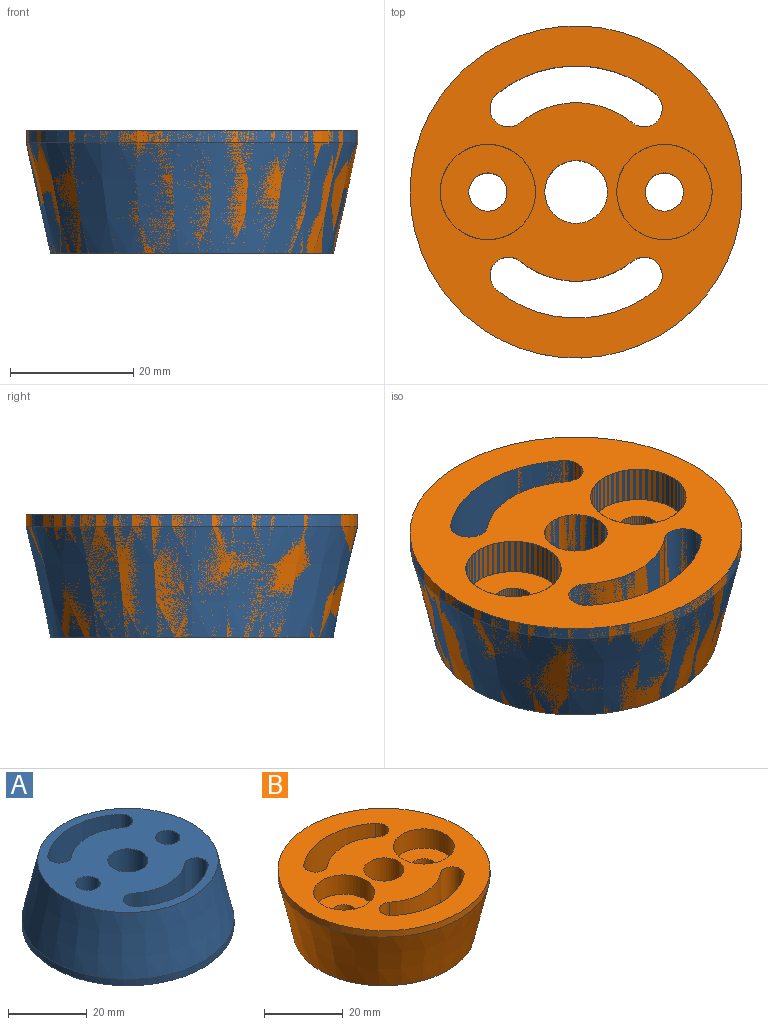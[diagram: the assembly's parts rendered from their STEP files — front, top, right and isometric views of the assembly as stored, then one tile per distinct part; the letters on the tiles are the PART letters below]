
ASSEMBLY  parts=2 mates=1
PART A: 37 faces, bbox 54x54x20 mm
  f0: plane 54x54mm, normal (0,0,-1), area 1488.9mm2, adj f6,f7,f25,f26,f27,f28,f29,f30
  f1: cylinder r=3.1mm len=6.2mm, axis (0,0,1), area 72.1mm2, adj f24,f36
  f2: cylinder r=3.1mm len=6.2mm, axis (0,0,1), area 72.1mm2, adj f10,f33
  f3: cylinder r=3.1mm len=6.2mm, axis (0,0,1), area 97.4mm2, adj f5,f23
  f4: cylinder r=3.1mm len=6.2mm, axis (0,0,1), area 97.4mm2, adj f5,f9
  f5: plane 46x46mm, normal (0,0,1), area 1177.6mm2, adj f3,f4,f6,f8,f25,f26,f27,f28
  f6: cylinder r=5.1mm len=20mm, axis (0,0,-1), area 640.9mm2, adj f0,f5
  f7: cylinder r=27mm len=54mm, axis (0,0,-1), area 339.3mm2, adj f0,f8
  f8: cone r=27mm half-angle=12.5deg, axis (0,0,-1), area 2896.4mm2, adj f5,f7
  f9: plane 11.78x10.2mm, normal (0,0,-1), area 59.9mm2, adj f4,f11,f12,f13,f14,f15,f16
  f10: plane 11.78x10.2mm, normal (0,0,1), area 59.9mm2, adj f2,f11,f12,f13,f14,f15,f16
  f11: plane 5.89x5.3mm, normal (-1,0,0), area 31.2mm2, adj f9,f10,f12,f16
  f12: plane 5.3x5.1mm, normal (-0.5,0.87,0), area 31.2mm2, adj f9,f10,f11,f13
  f13: plane 5.3x5.1mm, normal (0.5,0.87,0), area 31.2mm2, adj f9,f10,f12,f14
  f14: plane 5.89x5.3mm, normal (1,0,0), area 31.2mm2, adj f9,f10,f13,f15
  f15: plane 5.3x5.1mm, normal (0.5,-0.87,0), area 31.2mm2, adj f9,f10,f14,f16
  f16: plane 5.3x5.1mm, normal (-0.5,-0.87,0), area 31.2mm2, adj f9,f10,f11,f15
  f17: plane 5.3x5.1mm, normal (-0.5,-0.87,0), area 31.2mm2, adj f18,f22,f23,f24
  f18: plane 5.89x5.3mm, normal (-1,0,0), area 31.2mm2, adj f17,f19,f23,f24
  f19: plane 5.3x5.1mm, normal (-0.5,0.87,0), area 31.2mm2, adj f18,f20,f23,f24
  f20: plane 5.3x5.1mm, normal (0.5,0.87,0), area 31.2mm2, adj f19,f21,f23,f24
  f21: plane 5.89x5.3mm, normal (1,0,0), area 31.2mm2, adj f20,f22,f23,f24
  f22: plane 5.3x5.1mm, normal (0.5,-0.87,0), area 31.2mm2, adj f17,f21,f23,f24
  f23: plane 11.78x10.2mm, normal (0,0,-1), area 59.9mm2, adj f3,f17,f18,f19,f20,f21,f22
  f24: plane 11.78x10.2mm, normal (0,0,1), area 59.9mm2, adj f1,f17,f18,f19,f20,f21,f22
  f25: cylinder r=14.5mm len=20mm, axis (0,0,-1), area 394.5mm2, adj f0,f5,f26,f28
  f26: cylinder r=3mm len=20mm, axis (0,0,-1), area 188.5mm2, adj f0,f5,f25,f27
  f27: cylinder r=20.5mm len=25.79mm, axis (0,0,-1), area 557.8mm2, adj f0,f5,f26,f28
  f28: cylinder r=3mm len=20mm, axis (0,0,-1), area 188.5mm2, adj f0,f5,f25,f27
  f29: cylinder r=14.5mm len=20mm, axis (0,0,-1), area 394.5mm2, adj f0,f5,f30,f32
  f30: cylinder r=3mm len=20mm, axis (0,0,-1), area 188.5mm2, adj f0,f5,f29,f31
  f31: cylinder r=20.5mm len=25.79mm, axis (0,0,-1), area 557.8mm2, adj f0,f5,f30,f32
  f32: cylinder r=3mm len=20mm, axis (0,0,-1), area 188.5mm2, adj f0,f5,f29,f31
  f33: plane 15.5x15.5mm, normal (0,0,-1), area 158.5mm2, adj f2,f34
  f34: cylinder r=7.75mm len=15.5mm, axis (0,0,-1), area 292.2mm2, adj f0,f33
  f35: cylinder r=7.75mm len=15.5mm, axis (0,0,-1), area 292.2mm2, adj f0,f36
  f36: plane 15.5x15.5mm, normal (0,0,-1), area 158.5mm2, adj f1,f35
PART B: 19 faces, bbox 54x54x20 mm
  f0: plane 54x54mm, normal (0,0,1), area 1488.9mm2, adj f4,f6,f7,f8,f9,f10,f11,f12
  f1: cylinder r=3.1mm len=14mm, axis (0,0,1), area 272.7mm2, adj f3,f18
  f2: cylinder r=3.1mm len=14mm, axis (0,0,1), area 272.7mm2, adj f3,f15
  f3: plane 46x46mm, normal (0,0,-1), area 1177.6mm2, adj f1,f2,f4,f5,f7,f8,f9,f10
  f4: cylinder r=5.1mm len=20mm, axis (0,0,-1), area 640.9mm2, adj f0,f3
  f5: cone r=27mm half-angle=12.5deg, axis (0,0,1), area 2896.4mm2, adj f3,f6
  f6: cylinder r=27mm len=54mm, axis (0,0,-1), area 339.3mm2, adj f0,f5
  f7: cylinder r=14.5mm len=20mm, axis (0,0,-1), area 394.5mm2, adj f0,f3,f8,f10
  f8: cylinder r=3mm len=20mm, axis (0,0,-1), area 188.5mm2, adj f0,f3,f7,f9
  f9: cylinder r=20.5mm len=25.79mm, axis (0,0,-1), area 557.8mm2, adj f0,f3,f8,f10
  f10: cylinder r=3mm len=20mm, axis (0,0,-1), area 188.5mm2, adj f0,f3,f7,f9
  f11: cylinder r=14.5mm len=20mm, axis (0,0,-1), area 394.5mm2, adj f0,f3,f12,f14
  f12: cylinder r=3mm len=20mm, axis (0,0,-1), area 188.5mm2, adj f0,f3,f11,f13
  f13: cylinder r=20.5mm len=25.79mm, axis (0,0,-1), area 557.8mm2, adj f0,f3,f12,f14
  f14: cylinder r=3mm len=20mm, axis (0,0,-1), area 188.5mm2, adj f0,f3,f11,f13
  f15: plane 15.5x15.5mm, normal (0,0,1), area 158.5mm2, adj f2,f16
  f16: cylinder r=7.75mm len=15.5mm, axis (0,0,1), area 292.2mm2, adj f0,f15
  f17: cylinder r=7.75mm len=15.5mm, axis (0,0,1), area 292.2mm2, adj f0,f18
  f18: plane 15.5x15.5mm, normal (0,0,1), area 158.5mm2, adj f1,f17
PLACE A rot(axis=(1,0,0),180deg) t=(-13.11,7.75,32.99)mm
PLACE B t=(-13.11,7.75,-53.01)mm
MATE slider A.f6 <-> B.f4  axis (0,0,1) through (-13.11,7.75,32.99)mm
